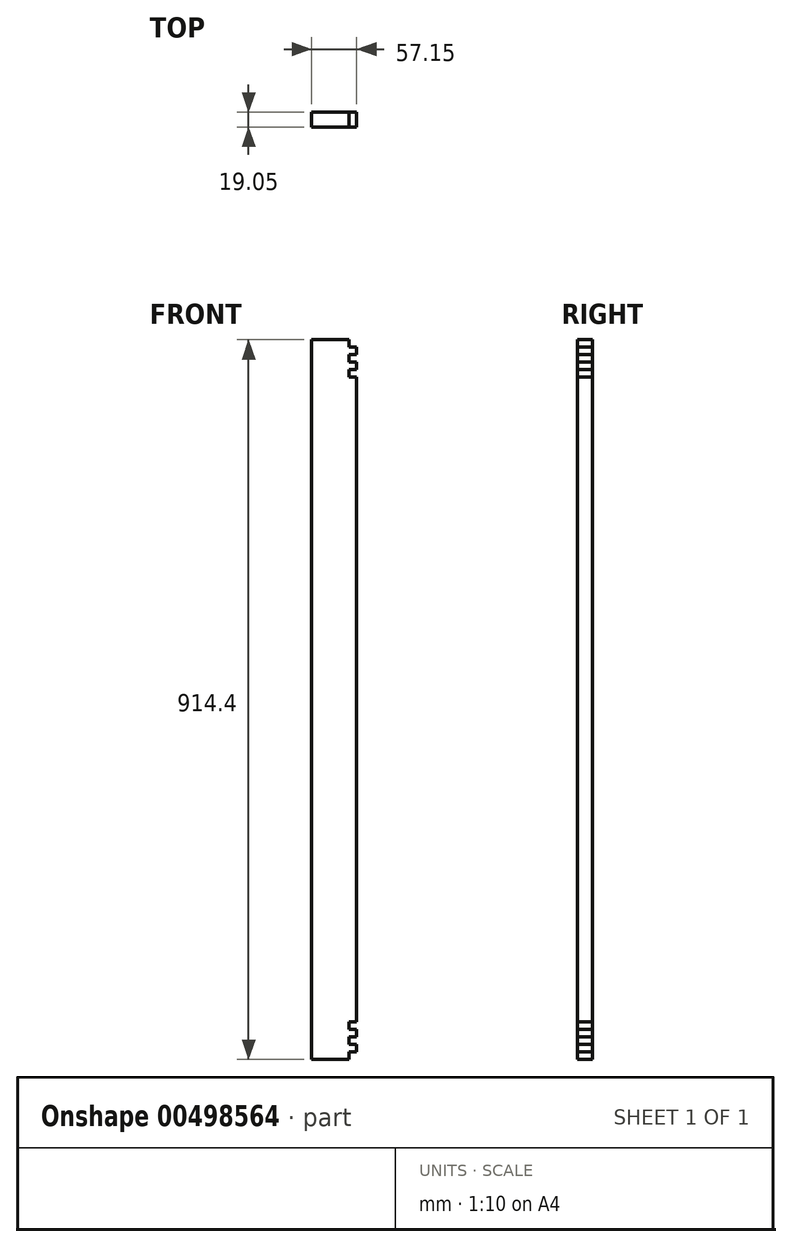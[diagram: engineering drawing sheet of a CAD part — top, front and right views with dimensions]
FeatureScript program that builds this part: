
annotation { "Feature Type Name" : "Feature", "Feature Type Description" : "" }
export const myFeature = defineFeature(function(context is Context, id is Id, definition is map)
    precondition{}
    {
        {
            var Q0;
            Q0=qCreatedBy(makeId("Front.planeOp"),FACE);
            var sketch = newSketch(context, id + "F0", { "sketchPlane" : qUnion([Q0])});
            skLineSegment(sketch, "E0.bottom", {"start": v(0, 0) * mm, "end": v(57.15, 0) * mm});
            skLineSegment(sketch, "E0.top", {"start": v(0, 914.4) * mm, "end": v(57.15, 914.4) * mm});
            skLineSegment(sketch, "E0.left", {"start": v(0, 0) * mm, "end": v(0, 914.4) * mm});
            skLineSegment(sketch, "E0.right", {"start": v(57.15, 0) * mm, "end": v(57.15, 914.4) * mm});
            skSolve(sketch);
        }
        {
            var Q0;
            Q0 = qSketchRegion(id + "F0", true);
            extrude(context, id + "F1", {"entities" : qUnion([Q0]), "depth" : 19.05 * mm, "offsetDistance" : 25.4 * mm});
        }
        {
            var Q0;
            Q0=makeQuery(id+"F1.opExtrude","CAP_FACE",FACE,{"disambiguationData":[OSD([sQuery(id+"F0.wireOp",EDGE,"E0.bottom"),sQuery(id+"F0.wireOp",EDGE,"E0.top"),sQuery(id+"F0.wireOp",EDGE,"E0.left"),sQuery(id+"F0.wireOp",EDGE,"E0.right")])],"isStart":false});
            var sketch = newSketch(context, id + "F2", { "sketchPlane" : qUnion([Q0])});
            skLineSegment(sketch, "E1.bottom", {"start": v(57.15, 914.4) * mm, "end": v(47.62, 914.4) * mm});
            skLineSegment(sketch, "E1.top", {"start": v(57.15, 904.88) * mm, "end": v(47.62, 904.88) * mm});
            skLineSegment(sketch, "E1.left", {"start": v(57.15, 914.4) * mm, "end": v(57.15, 904.88) * mm});
            skLineSegment(sketch, "E1.right", {"start": v(47.62, 914.4) * mm, "end": v(47.62, 904.88) * mm});
            skLineSegment(sketch, "E2.bottom", {"start": v(57.15, 895.35) * mm, "end": v(47.62, 895.35) * mm});
            skLineSegment(sketch, "E2.top", {"start": v(57.15, 885.83) * mm, "end": v(47.62, 885.83) * mm});
            skLineSegment(sketch, "E2.left", {"start": v(57.15, 895.35) * mm, "end": v(57.15, 885.83) * mm});
            skLineSegment(sketch, "E2.right", {"start": v(47.62, 895.35) * mm, "end": v(47.62, 885.83) * mm});
            skLineSegment(sketch, "E3.bottom", {"start": v(57.15, 876.3) * mm, "end": v(47.62, 876.3) * mm});
            skLineSegment(sketch, "E3.top", {"start": v(57.15, 866.78) * mm, "end": v(47.62, 866.78) * mm});
            skLineSegment(sketch, "E3.left", {"start": v(57.15, 876.3) * mm, "end": v(57.15, 866.78) * mm});
            skLineSegment(sketch, "E3.right", {"start": v(47.62, 876.3) * mm, "end": v(47.62, 866.78) * mm});
            skLineSegment(sketch, "E4.bottom", {"start": v(57.15, 47.63) * mm, "end": v(47.63, 47.63) * mm});
            skLineSegment(sketch, "E4.top", {"start": v(57.15, 38.1) * mm, "end": v(47.63, 38.1) * mm});
            skLineSegment(sketch, "E4.left", {"start": v(57.15, 47.63) * mm, "end": v(57.15, 38.1) * mm});
            skLineSegment(sketch, "E4.right", {"start": v(47.63, 47.63) * mm, "end": v(47.63, 38.1) * mm});
            skLineSegment(sketch, "E5.bottom", {"start": v(57.15, 28.58) * mm, "end": v(47.63, 28.58) * mm});
            skLineSegment(sketch, "E5.top", {"start": v(57.15, 19.05) * mm, "end": v(47.63, 19.05) * mm});
            skLineSegment(sketch, "E5.left", {"start": v(57.15, 28.58) * mm, "end": v(57.15, 19.05) * mm});
            skLineSegment(sketch, "E5.right", {"start": v(47.63, 28.58) * mm, "end": v(47.63, 19.05) * mm});
            skLineSegment(sketch, "E6.bottom", {"start": v(57.15, 9.53) * mm, "end": v(47.63, 9.53) * mm});
            skLineSegment(sketch, "E6.top", {"start": v(57.15, 0) * mm, "end": v(47.63, 0) * mm});
            skLineSegment(sketch, "E6.left", {"start": v(57.15, 9.53) * mm, "end": v(57.15, 0) * mm});
            skLineSegment(sketch, "E6.right", {"start": v(47.63, 9.53) * mm, "end": v(47.63, 0) * mm});
            skSolve(sketch);
        }
        {
            var Q0;
            Q0 = qSketchRegion(id + "F2", true);
            extrude(context, id + "F3", {"entities" : qUnion([Q0]), "operationType" : NewBodyOperationType.REMOVE, "endBound" : BoundingType.THROUGH_ALL, "oppositeDirection" : true, "depth" : 25.4 * mm, "offsetDistance" : 25.4 * mm});
        }
    });
